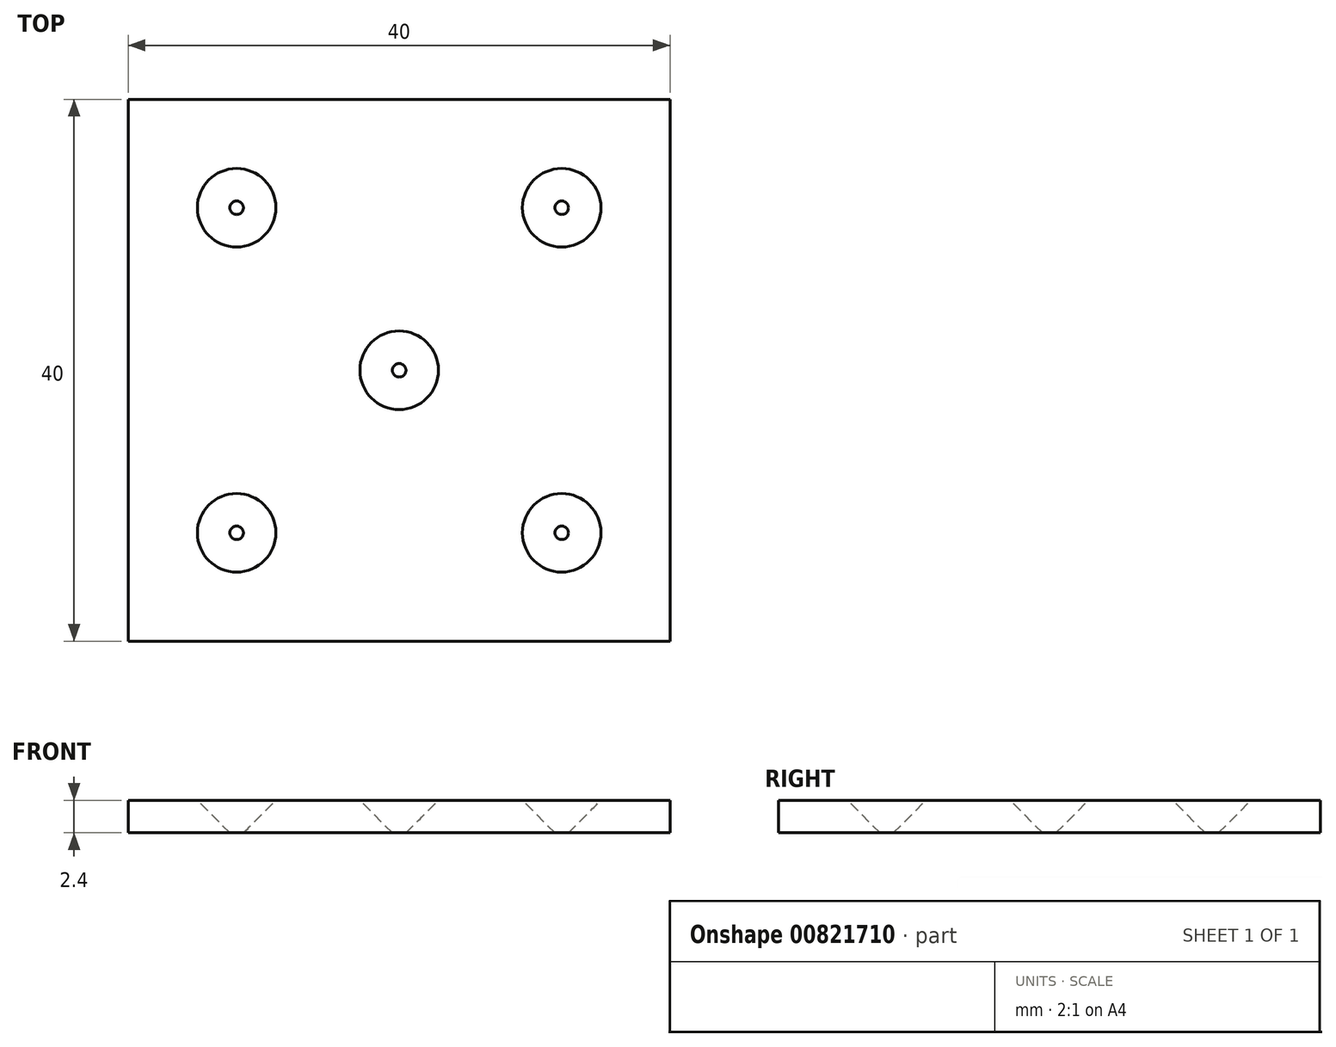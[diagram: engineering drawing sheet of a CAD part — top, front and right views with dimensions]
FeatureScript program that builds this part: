
annotation { "Feature Type Name" : "Feature", "Feature Type Description" : "" }
export const myFeature = defineFeature(function(context is Context, id is Id, definition is map)
    precondition{}
    {
        {
            var Q0;
            Q0=qCreatedBy(makeId("Top.planeOp"),FACE);
            var sketch = newSketch(context, id + "F0", { "sketchPlane" : qUnion([Q0])});
            skLineSegment(sketch, "E0.bottom", {"start": v(-20, 20) * mm, "end": v(20, 20) * mm});
            skLineSegment(sketch, "E0.top", {"start": v(-20, -20) * mm, "end": v(20, -20) * mm});
            skLineSegment(sketch, "E0.left", {"start": v(-20, 20) * mm, "end": v(-20, -20) * mm});
            skLineSegment(sketch, "E0.right", {"start": v(20, 20) * mm, "end": v(20, -20) * mm});
            skPoint(sketch, "E0.middle", {"position": v(0, 0) * mm});
            skCircle(sketch, "E1", {"center": v(-12, 12) * mm, "radius": 0.4 * mm});
            skCircle(sketch, "E2.MirrorC", {"center": v(12, 12) * mm, "radius": 0.4 * mm});
            skCircle(sketch, "E3.MirrorC", {"center": v(12, -12) * mm, "radius": 0.4 * mm});
            skCircle(sketch, "E4.MirrorC", {"center": v(-12, -12) * mm, "radius": 0.4 * mm});
            skCircle(sketch, "E5", {"center": v(0, 0) * mm, "radius": 0.4 * mm});
            skSolve(sketch);
        }
        {
            var Q0;
            Q0 = qSketchRegion(id + "F0", true);
            extrude(context, id + "F1", {"entities" : qUnion([Q0]), "depth" : 2.4 * mm, "offsetDistance" : 25 * mm});
        }
        {
            var Q0;
            Q0=makeQuery(id+"F1.opExtrude","CAP_EDGE",EDGE,{"disambiguationData":[OSD([sQuery(id+"F0.wireOp",EDGE,"E1")])],"isStart":false});
            var Q1;
            Q1=makeQuery(id+"F1.opExtrude","CAP_EDGE",EDGE,{"disambiguationData":[OSD([sQuery(id+"F0.wireOp",EDGE,"E2.MirrorC")])],"isStart":false});
            var Q2;
            Q2=makeQuery(id+"F1.opExtrude","CAP_EDGE",EDGE,{"disambiguationData":[OSD([sQuery(id+"F0.wireOp",EDGE,"E3.MirrorC")])],"isStart":false});
            var Q3;
            Q3=makeQuery(id+"F1.opExtrude","CAP_EDGE",EDGE,{"disambiguationData":[OSD([sQuery(id+"F0.wireOp",EDGE,"E4.MirrorC")])],"isStart":false});
            var Q4;
            Q4=makeQuery(id+"F1.opExtrude","CAP_EDGE",EDGE,{"disambiguationData":[OSD([sQuery(id+"F0.wireOp",EDGE,"E5")])],"isStart":false});
            chamfer(context, id + "F2", {"entities" : qUnion([Q0, Q1, Q2, Q3, Q4]), "width" : 2.5 * mm, "tangentPropagation" : true});
        }
    });
